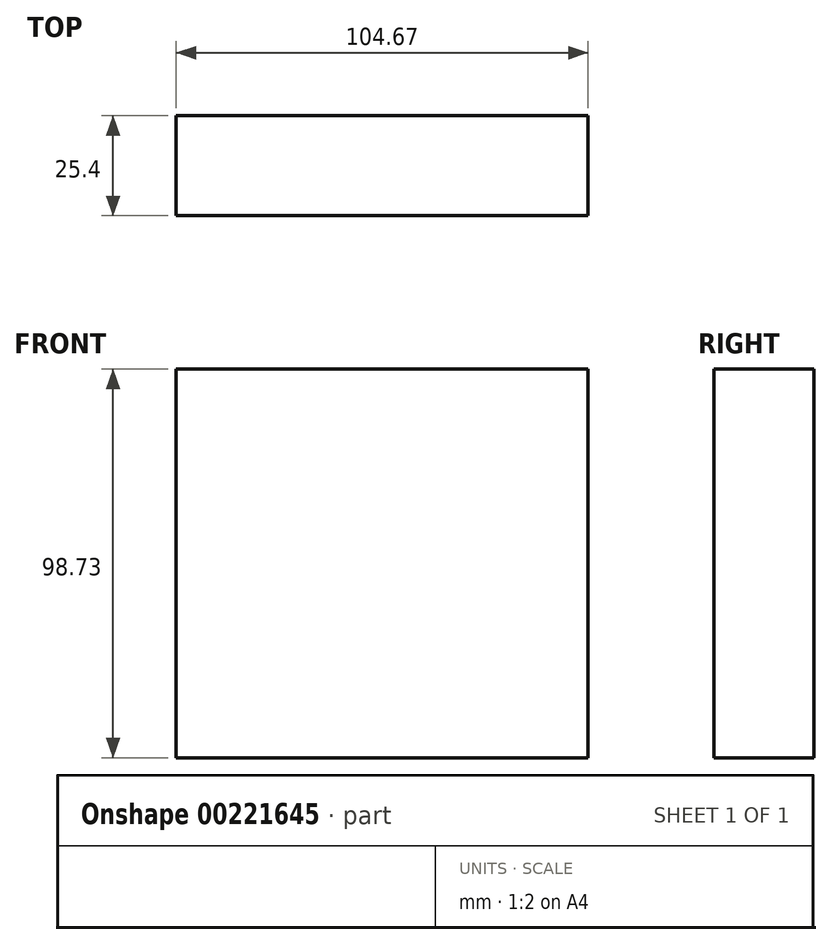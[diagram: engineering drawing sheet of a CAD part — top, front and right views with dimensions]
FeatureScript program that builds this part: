
annotation { "Feature Type Name" : "Feature", "Feature Type Description" : "" }
export const myFeature = defineFeature(function(context is Context, id is Id, definition is map)
    precondition{}
    {
        {
            var Q0;
            Q0=qCreatedBy(makeId("Front.planeOp"),FACE);
            var sketch = newSketch(context, id + "F0", { "sketchPlane" : qUnion([Q0])});
            skLineSegment(sketch, "E0.bottom", {"start": v(-122.88, 121.16) * mm, "end": v(-18.21, 121.16) * mm});
            skLineSegment(sketch, "E0.top", {"start": v(-122.88, 22.43) * mm, "end": v(-18.21, 22.43) * mm});
            skLineSegment(sketch, "E0.left", {"start": v(-122.88, 121.16) * mm, "end": v(-122.88, 22.43) * mm});
            skLineSegment(sketch, "E0.right", {"start": v(-18.21, 121.16) * mm, "end": v(-18.21, 22.43) * mm});
            skPoint(sketch, "E0.middle", {"position": v(-70.55, 71.8) * mm});
            skSolve(sketch);
        }
        {
            var Q0;
            Q0=makeQuery(id+"F0.imprint","IMPRINT",FACE,{"disambiguationData":[TD([[makeQuery(id+"F0.imprint","IMPRINT",EDGE,{"derivedFrom":sQuery(id+"F0.wireOp",EDGE,"E0.bottom")}),-1.0]])]});
            extrude(context, id + "F1", {"entities" : qUnion([Q0]), "depth" : 25.4 * mm});
        }
    });
